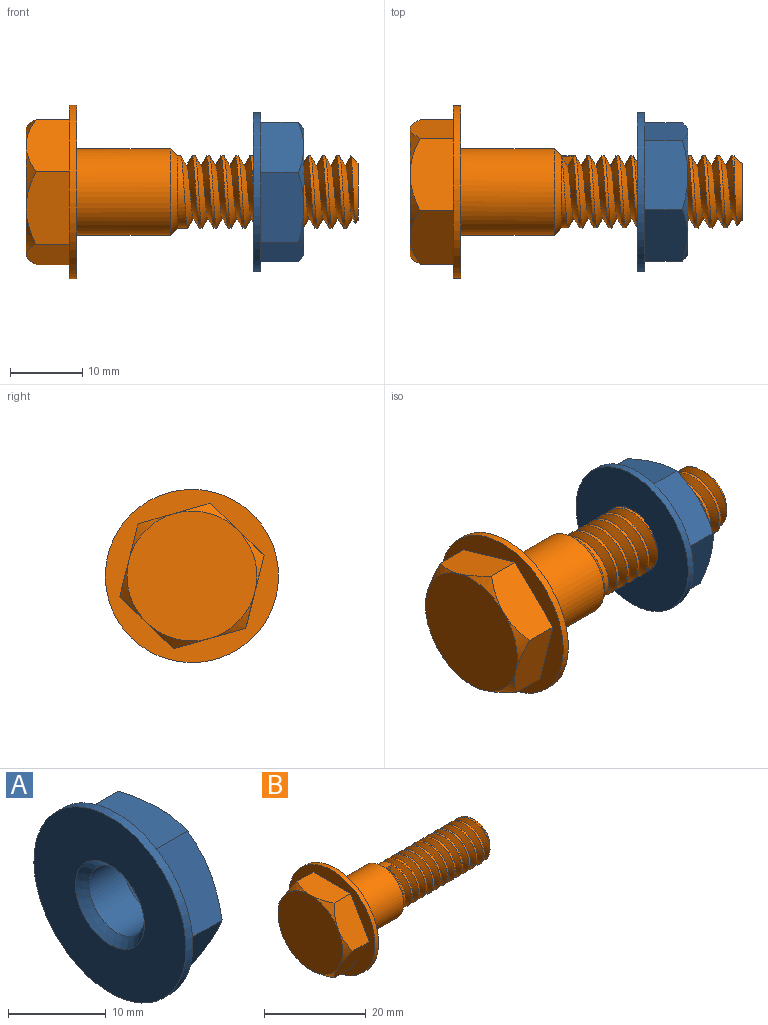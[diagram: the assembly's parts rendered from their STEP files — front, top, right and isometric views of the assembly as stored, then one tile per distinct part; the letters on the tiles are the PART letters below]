
ASSEMBLY  parts=2 mates=1
PART A: 19 faces, bbox 7.8x22.8x22.8 mm
  f0: plane 17.32x17.32mm, normal (1,0,0), area 157.1mm2, adj f8,f9,f10,f11,f12,f13,f14
  f1: plane 9.48x6.83mm, normal (0,-0.87,0.5), area 57.3mm2, adj f2,f6,f9,f13,f15
  f2: plane 9.48x6.83mm, normal (0,-0.87,-0.5), area 57.3mm2, adj f1,f3,f12,f13,f15
  f3: plane 10.83x6.83mm, normal (0,0,-1), area 57.3mm2, adj f2,f4,f11,f12,f15
  f4: plane 9.48x6.83mm, normal (0,0.87,-0.5), area 57.3mm2, adj f3,f5,f10,f11,f15
  f5: plane 9.48x6.83mm, normal (0,0.87,0.5), area 57.3mm2, adj f4,f6,f8,f10,f15
  f6: plane 10.83x6.83mm, normal (0,0,1), area 57.3mm2, adj f1,f5,f8,f9,f15
  f7: cylinder r=4mm len=8mm, axis (1,0,0), area 125.7mm2, adj f14,f18
  f8: cone r=8.66mm half-angle=60deg, axis (-1,0,0), area 7.4mm2, adj f0,f5,f6
  f9: cone r=8.66mm half-angle=60deg, axis (-1,0,0), area 7.4mm2, adj f0,f1,f6
  f10: cone r=8.66mm half-angle=60deg, axis (-1,0,0), area 7.4mm2, adj f0,f4,f5
  f11: cone r=8.66mm half-angle=60deg, axis (-1,0,0), area 7.4mm2, adj f0,f3,f4
  f12: cone r=8.66mm half-angle=60deg, axis (-1,0,0), area 7.4mm2, adj f0,f2,f3
  f13: cone r=8.66mm half-angle=60deg, axis (-1,0,0), area 7.4mm2, adj f0,f1,f2
  f14: cone r=4mm half-angle=45deg, axis (1,0,0), area 40mm2, adj f0,f7
  f15: plane 22x22mm, normal (1,0,0), area 120.3mm2, adj f1,f2,f3,f4,f5,f6,f16
  f16: cylinder r=11mm len=22mm, axis (1,0,0), area 69.1mm2, adj f15,f17
  f17: plane 22x22mm, normal (-1,0,0), area 301.6mm2, adj f16,f18
  f18: cone r=5mm half-angle=45deg, axis (-1,0,0), area 40mm2, adj f7,f17
PART B: 25 faces, bbox 47.6x25x25 mm
  f0: cylinder r=5mm len=24mm, axis (-1,0,0), area 53.3mm2, adj f3,f4,f6,f7,f8
  f1: cylinder r=6mm len=13mm, axis (-1,0,0), area 490.1mm2, adj f4,f10
  f2: plane 8x8mm, normal (1,0,0), area 50.3mm2, adj f3,f5,f8
  f3: cone r=4mm half-angle=45deg, axis (-1,0,0), area 23mm2, adj f0,f2,f5,f8
  f4: cone r=5mm half-angle=45deg, axis (-1,0,0), area 48.9mm2, adj f0,f1
  f5: plane 1.39x1mm, normal (0,1,0), area 0.3mm2, adj f2,f3,f7,f8
  f6: plane 1.6x1.39mm, normal (0,-1,0), area 1.1mm2, adj f0,f7,f8
  f7: bspline ~24.8x10mm, area 497.3mm2, adj f0,f5,f6,f8
  f8: bspline ~24.8x9.99mm, area 505.7mm2, adj f0,f2,f3,f5,f6,f7
  f9: cylinder r=12mm len=24mm, axis (-1,0,0), area 75.4mm2, adj f10,f11
  f10: plane 24x24mm, normal (1,0,0), area 339.3mm2, adj f1,f9
  f11: plane 24x24mm, normal (-1,0,0), area 171.8mm2, adj f9,f19,f20,f21,f22,f23,f24
  f12: plane 18x18mm, normal (-1,0,0), area 254.5mm2, adj f13,f14,f15,f16,f17,f18
  f13: cone r=9mm half-angle=45deg, axis (1,0,0), area 9.8mm2, adj f12,f23,f24
  f14: cone r=9mm half-angle=45deg, axis (1,0,0), area 9.8mm2, adj f12,f22,f23
  f15: cone r=9mm half-angle=45deg, axis (1,0,0), area 9.8mm2, adj f12,f21,f22
  f16: cone r=9mm half-angle=45deg, axis (1,0,0), area 9.8mm2, adj f12,f20,f21
  f17: cone r=9mm half-angle=45deg, axis (1,0,0), area 9.8mm2, adj f12,f19,f20
  f18: cone r=9mm half-angle=45deg, axis (1,0,0), area 9.8mm2, adj f12,f19,f24
  f19: plane 11.42x7.02mm, normal (0,0,-1), area 57.4mm2, adj f11,f17,f18,f20,f24
  f20: plane 10.01x7.02mm, normal (0,0.87,-0.5), area 57.4mm2, adj f11,f16,f17,f19,f21
  f21: plane 10.01x7.02mm, normal (0,0.87,0.5), area 57.4mm2, adj f11,f15,f16,f20,f22
  f22: plane 11.42x7.02mm, normal (0,0,1), area 57.4mm2, adj f11,f14,f15,f21,f23
  f23: plane 10.01x7.02mm, normal (0,-0.87,0.5), area 57.4mm2, adj f11,f13,f14,f22,f24
  f24: plane 10.01x7.02mm, normal (0,-0.87,-0.5), area 57.4mm2, adj f11,f13,f18,f19,f23
PLACE A rot(axis=(-1,0,0),75.8deg) t=(97.71,9.29,-34.74)mm
PLACE B rot(axis=(-1,0,0),75.8deg) t=(65.21,9.29,-34.74)mm
MATE cylindrical A.f16 <-> B.f0  axis (1,0,0) through (91.71,9.29,-34.74)mm
